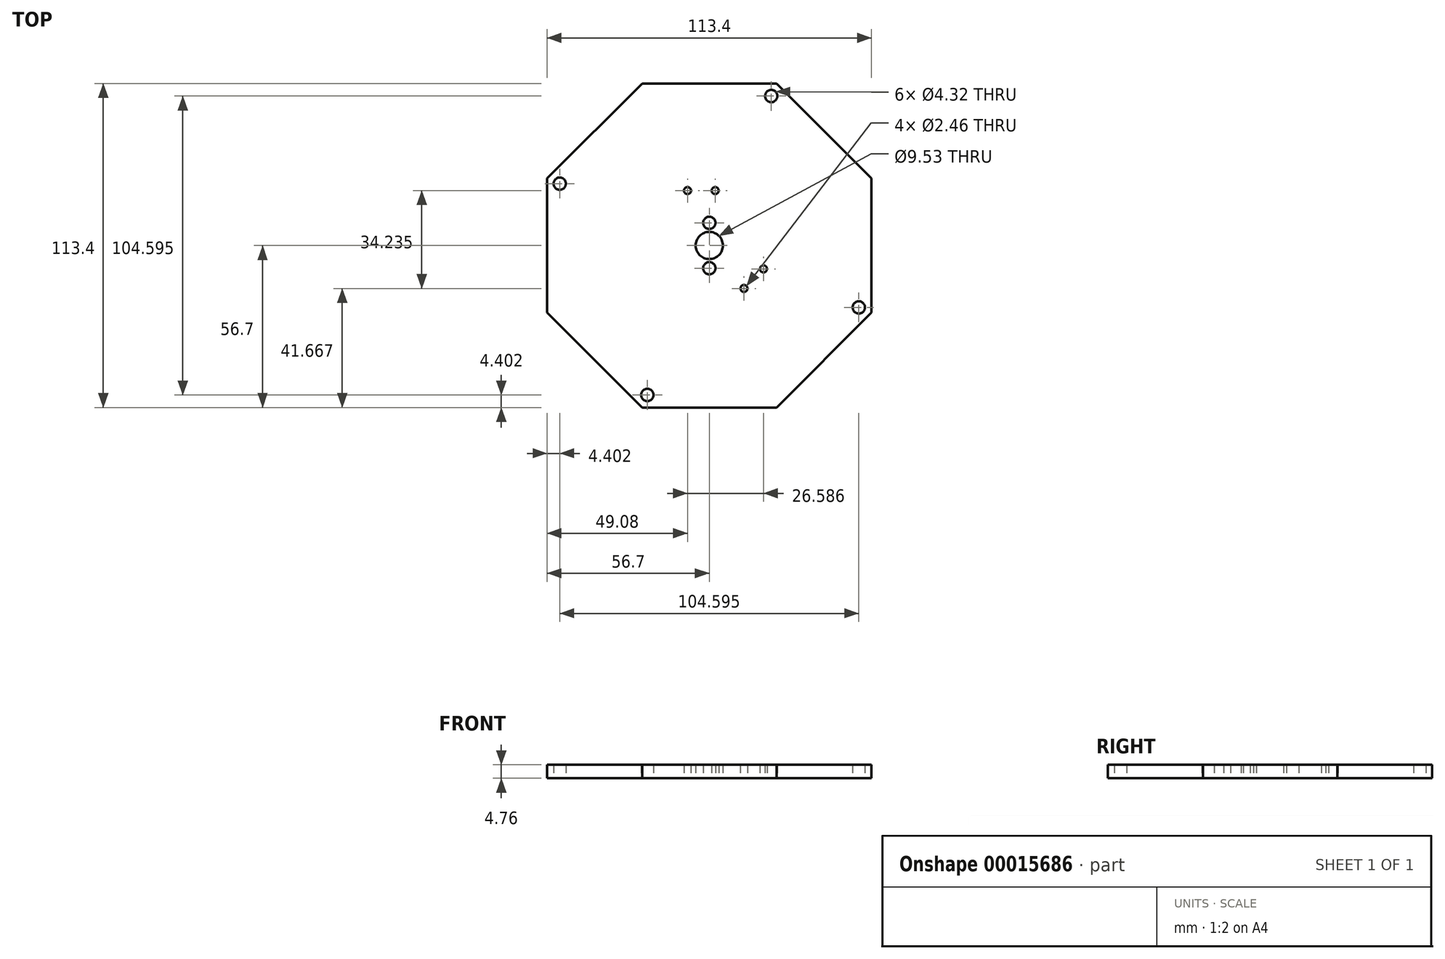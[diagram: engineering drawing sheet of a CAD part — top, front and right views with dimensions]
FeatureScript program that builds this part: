
annotation { "Feature Type Name" : "Feature", "Feature Type Description" : "" }
export const myFeature = defineFeature(function(context is Context, id is Id, definition is map)
    precondition{}
    {
        {
            var Q0;
            Q0=qCreatedBy(makeId("Top.planeOp"),FACE);
            var sketch = newSketch(context, id + "F0", { "sketchPlane" : qUnion([Q0])});
            skCircle(sketch, "E0.cCircle", {"center": v(0, 0) * mm, "radius": 56.7 * mm, "construction": true});
            skLineSegment(sketch, "E0.0", {"start": v(23.48, -56.7) * mm, "end": v(-23.48, -56.7) * mm});
            skLineSegment(sketch, "E0.1", {"start": v(-23.48, -56.7) * mm, "end": v(-56.7, -23.48) * mm});
            skLineSegment(sketch, "E0.2", {"start": v(-56.7, -23.48) * mm, "end": v(-56.7, 23.48) * mm});
            skLineSegment(sketch, "E0.3", {"start": v(-56.7, 23.48) * mm, "end": v(-23.48, 56.7) * mm});
            skLineSegment(sketch, "E0.4", {"start": v(-23.48, 56.7) * mm, "end": v(23.48, 56.7) * mm});
            skLineSegment(sketch, "E0.5", {"start": v(23.48, 56.7) * mm, "end": v(56.7, 23.48) * mm});
            skLineSegment(sketch, "E0.6", {"start": v(56.7, 23.48) * mm, "end": v(56.7, -23.48) * mm});
            skLineSegment(sketch, "E0.7", {"start": v(56.7, -23.48) * mm, "end": v(23.48, -56.7) * mm});
            skPoint(sketch, "E0.0.midPoint", {"position": v(0, -56.7) * mm});
            skLineSegment(sketch, "E1", {"start": v(-23.48, -56.7) * mm, "end": v(-21.66, -52.3) * mm});
            skLineSegment(sketch, "E2", {"start": v(-21.66, -52.3) * mm, "end": v(0, 0) * mm});
            skLineSegment(sketch, "E3", {"start": v(0, 0) * mm, "end": v(52.3, -21.66) * mm, "construction": true});
            skLineSegment(sketch, "E4", {"start": v(52.3, -21.66) * mm, "end": v(56.7, -23.48) * mm, "construction": true});
            skLineSegment(sketch, "E5", {"start": v(0, 0) * mm, "end": v(-52.3, 21.66) * mm, "construction": true});
            skLineSegment(sketch, "E6", {"start": v(-52.3, 21.66) * mm, "end": v(-56.7, 23.48) * mm, "construction": true});
            skLineSegment(sketch, "E7", {"start": v(0, 0) * mm, "end": v(21.66, 52.3) * mm, "construction": true});
            skLineSegment(sketch, "E8", {"start": v(21.66, 52.3) * mm, "end": v(23.48, 56.7) * mm, "construction": true});
            skCircle(sketch, "E9", {"center": v(-21.66, -52.3) * mm, "radius": 2.16 * mm});
            skCircle(sketch, "E10", {"center": v(52.3, -21.66) * mm, "radius": 2.16 * mm});
            skCircle(sketch, "E11", {"center": v(21.66, 52.3) * mm, "radius": 2.16 * mm});
            skCircle(sketch, "E12", {"center": v(-52.3, 21.66) * mm, "radius": 2.16 * mm});
            skLineSegment(sketch, "E13", {"start": v(0, 0) * mm, "end": v(0, 7.94) * mm});
            skLineSegment(sketch, "E14", {"start": v(0, 0) * mm, "end": v(0, -7.94) * mm});
            skCircle(sketch, "E15", {"center": v(0, 0) * mm, "radius": 4.76 * mm});
            skCircle(sketch, "E16", {"center": v(0, 7.94) * mm, "radius": 2.16 * mm});
            skCircle(sketch, "E17", {"center": v(0, -7.94) * mm, "radius": 2.16 * mm});
            skLineSegment(sketch, "E18", {"start": v(0, 56.7) * mm, "end": v(0, 19.2) * mm});
            skLineSegment(sketch, "E19", {"start": v(0, 19.2) * mm, "end": v(2.06, 19.2) * mm});
            skLineSegment(sketch, "E20", {"start": v(0, 19.2) * mm, "end": v(-7.62, 19.2) * mm});
            skLineSegment(sketch, "E21", {"start": v(13.58, -13.58) * mm, "end": v(12.12, -15.03) * mm});
            skLineSegment(sketch, "E22", {"start": v(13.58, -13.58) * mm, "end": v(18.97, -8.19) * mm});
            skCircle(sketch, "E23", {"center": v(2.06, 19.2) * mm, "radius": 1.23 * mm});
            skCircle(sketch, "E24", {"center": v(-7.62, 19.2) * mm, "radius": 1.23 * mm});
            skCircle(sketch, "E25", {"center": v(18.97, -8.19) * mm, "radius": 1.23 * mm});
            skCircle(sketch, "E26", {"center": v(12.12, -15.03) * mm, "radius": 1.23 * mm});
            skLineSegment(sketch, "E27", {"start": v(0, 19.2) * mm, "end": v(0, 7.94) * mm});
            skLineSegment(sketch, "E28", {"start": v(13.58, -13.58) * mm, "end": v(40.1, -40.1) * mm});
            skSolve(sketch);
        }
        {
            var Q0;
            Q0 = qSketchRegion(id + "F0", true);
            extrude(context, id + "F1", {"entities" : qUnion([Q0]), "depth" : 4.76 * mm});
        }
    });
